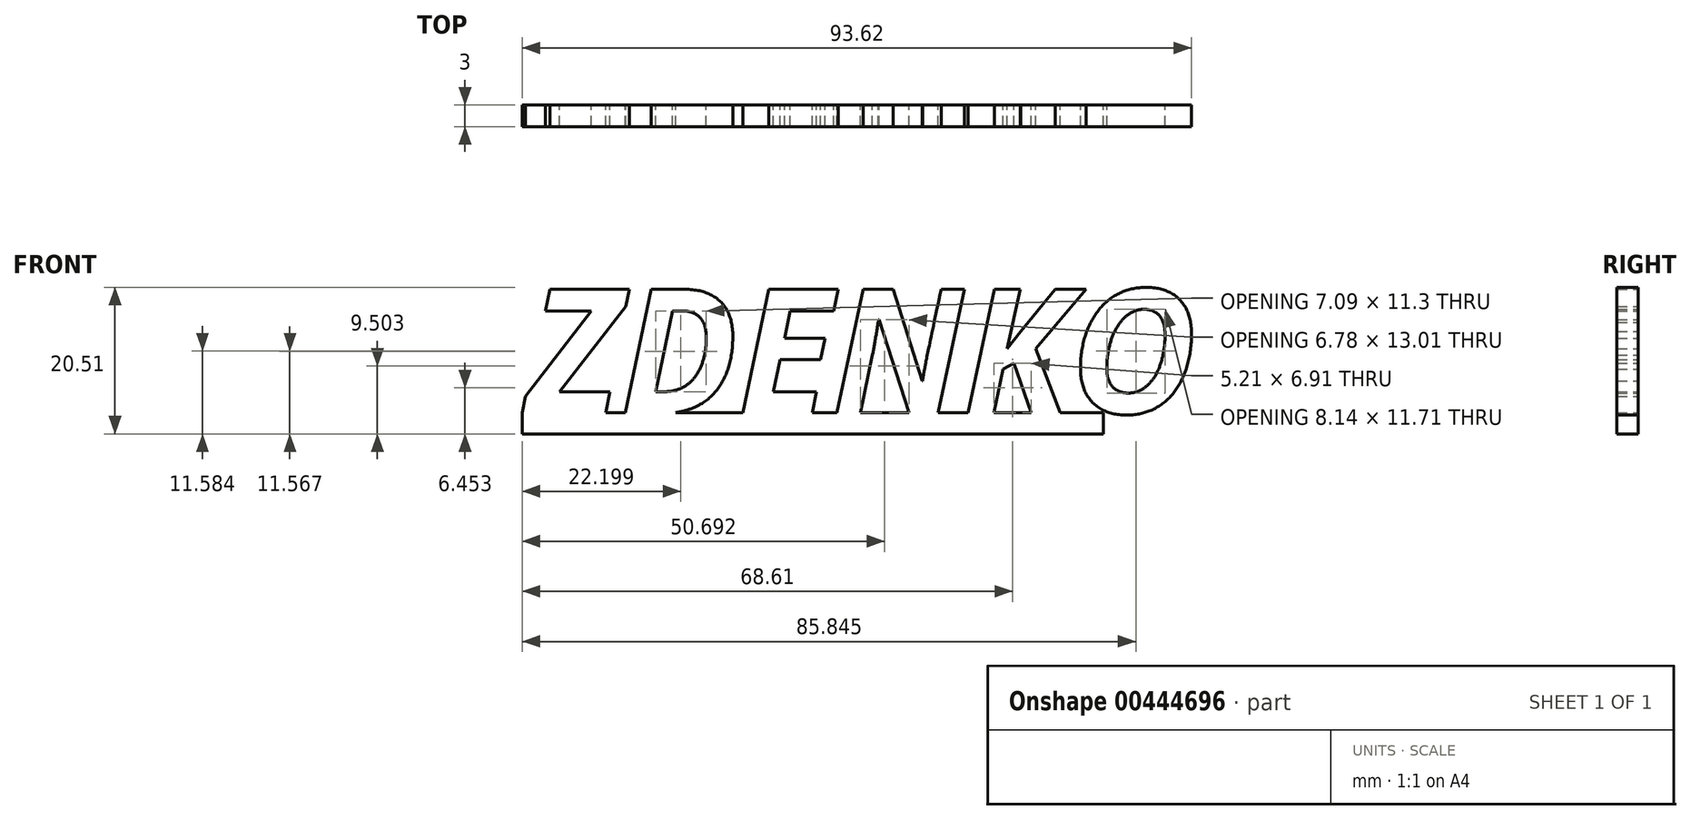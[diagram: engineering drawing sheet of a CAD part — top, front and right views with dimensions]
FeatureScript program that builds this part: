
annotation { "Feature Type Name" : "Feature", "Feature Type Description" : "" }
export const myFeature = defineFeature(function(context is Context, id is Id, definition is map)
    precondition{}
    {
        {
            var Q0;
            Q0=qCreatedBy(makeId("Front.planeOp"),FACE);
            var sketch = newSketch(context, id + "F0", { "sketchPlane" : qUnion([Q0])});
            skLineSegment(sketch, "E0.bottom", {"start": v(-45.46, 0) * mm, "end": v(35.81, 0) * mm});
            skLineSegment(sketch, "E0.top", {"start": v(-45.46, -3) * mm, "end": v(35.81, -3) * mm});
            skLineSegment(sketch, "E0.left", {"start": v(-45.46, 0) * mm, "end": v(-45.46, -3) * mm});
            skLineSegment(sketch, "E0.right", {"start": v(35.81, 0) * mm, "end": v(35.81, -3) * mm});
            skText(sketch, "E1", { "text": "ZDENKO", "fontName": "OpenSans-BoldItalic.ttf"});
            const initialGuessF0  = {"E1": [-0.04475, -0.00012, 1, 0, 0.0175]};
            skSetInitialGuess(sketch, initialGuessF0);
            skSolve(sketch);
        }
        {
            var Q0;
            Q0=qSketchRegion(id+"F0",true);
            extrude(context, id + "F1", {"entities" : qUnion([Q0]), "depth" : 3 * mm});
        }
    });
